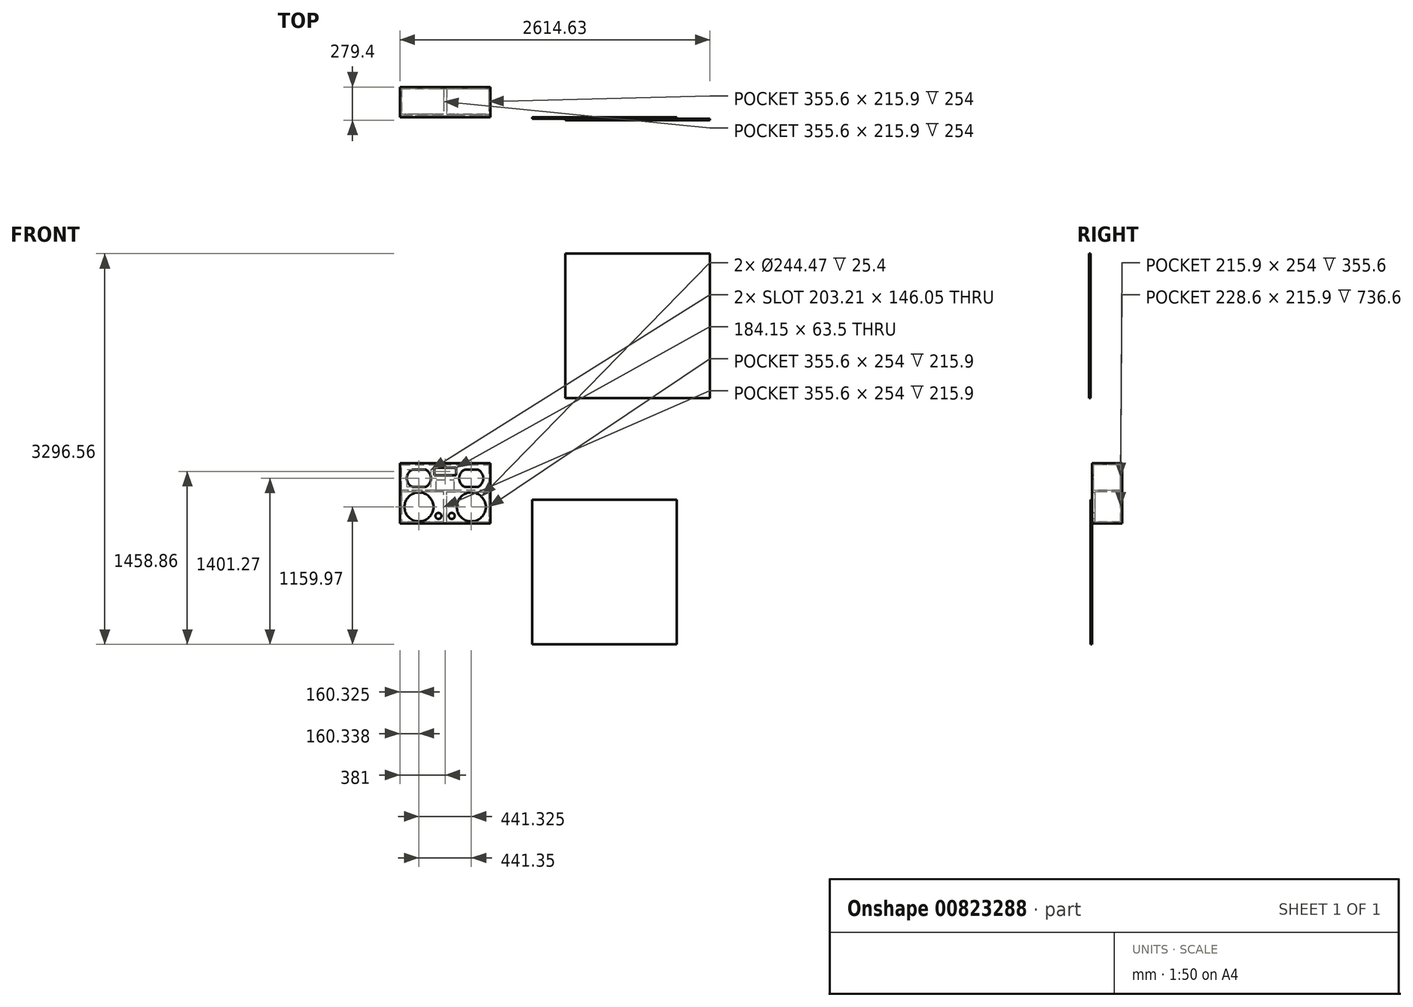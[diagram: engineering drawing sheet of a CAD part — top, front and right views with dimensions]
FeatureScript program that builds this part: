
annotation { "Feature Type Name" : "Feature", "Feature Type Description" : "" }
export const myFeature = defineFeature(function(context is Context, id is Id, definition is map)
    precondition{}
    {
        {
            var Q0;
            Q0=qCreatedBy(makeId("Front.planeOp"),FACE);
            var sketch = newSketch(context, id + "F0", { "sketchPlane" : qUnion([Q0])});
            skLineSegment(sketch, "E0.bottom", {"start": v(381, 254) * mm, "end": v(-381, 254) * mm});
            skLineSegment(sketch, "E0.top", {"start": v(381, -254) * mm, "end": v(-381, -254) * mm});
            skLineSegment(sketch, "E0.left", {"start": v(381, 254) * mm, "end": v(381, -254) * mm});
            skLineSegment(sketch, "E0.right", {"start": v(-381, 254) * mm, "end": v(-381, -254) * mm});
            skPoint(sketch, "E0.middle", {"position": v(0, 0) * mm});
            skSolve(sketch);
        }
        {
            var Q0;
            Q0 = qSketchRegion(id + "F0", true);
            extrude(context, id + "F1", {"entities" : qUnion([Q0]), "oppositeDirection" : true, "depth" : 12.7 * mm, "offsetDistance" : 25.4 * mm});
        }
        {
            var Q0;
            Q0=makeQuery(id+"F1.opExtrude","CAP_FACE",FACE,{"disambiguationData":[OSD([sQuery(id+"F0.wireOp",EDGE,"E0.bottom"),sQuery(id+"F0.wireOp",EDGE,"E0.top"),sQuery(id+"F0.wireOp",EDGE,"E0.left"),sQuery(id+"F0.wireOp",EDGE,"E0.right")])],"isStart":false});
            var sketch = newSketch(context, id + "F2", { "sketchPlane" : qUnion([Q0])});
            skLineSegment(sketch, "E1", {"start": v(368.3, 241.3) * mm, "end": v(-368.3, 241.3) * mm});
            skLineSegment(sketch, "E2", {"start": v(-381, 254) * mm, "end": v(-381, -254) * mm});
            skLineSegment(sketch, "E3", {"start": v(-381, -254) * mm, "end": v(381, -254) * mm});
            skLineSegment(sketch, "E4", {"start": v(381, -254) * mm, "end": v(381, 254) * mm});
            skLineSegment(sketch, "E5", {"start": v(381, 254) * mm, "end": v(-381, 254) * mm});
            skLineSegment(sketch, "E6", {"start": v(-12.7, -241.3) * mm, "end": v(-368.3, -241.3) * mm});
            skLineSegment(sketch, "E7", {"start": v(12.7, -241.3) * mm, "end": v(368.3, -241.3) * mm});
            skLineSegment(sketch, "E8", {"start": v(-368.3, 12.7) * mm, "end": v(-368.3, -241.3) * mm});
            skLineSegment(sketch, "E9", {"start": v(368.3, 12.7) * mm, "end": v(368.3, -241.3) * mm});
            skLineSegment(sketch, "E10", {"start": v(-12.7, -241.3) * mm, "end": v(-12.7, 12.7) * mm});
            skLineSegment(sketch, "E11", {"start": v(-12.7, 12.7) * mm, "end": v(-368.3, 12.7) * mm});
            skLineSegment(sketch, "E12", {"start": v(12.7, -241.3) * mm, "end": v(12.7, 12.7) * mm});
            skLineSegment(sketch, "E13", {"start": v(12.7, 12.7) * mm, "end": v(368.3, 12.7) * mm});
            skLineSegment(sketch, "E14", {"start": v(-368.3, 241.3) * mm, "end": v(-368.3, 25.4) * mm});
            skLineSegment(sketch, "E15", {"start": v(-368.3, 25.4) * mm, "end": v(368.3, 25.4) * mm});
            skLineSegment(sketch, "E16", {"start": v(368.3, 25.4) * mm, "end": v(368.3, 241.3) * mm});
            skSolve(sketch);
        }
        {
            var Q0;
            Q0 = qSketchRegion(id + "F2", true);
            extrude(context, id + "F3", {"entities" : qUnion([Q0]), "operationType" : NewBodyOperationType.ADD, "depth" : 228.6 * mm, "offsetDistance" : 25.4 * mm});
        }
        {
            var Q0;
            Q0=makeQuery(id+"F3.boolean.opBoolean","SPLIT",FACE,{"disambiguationData":[TD([makeQuery(id+"F3.opExtrude","SWEPT_FACE",FACE,{"disambiguationData":[OSD([sQuery(id+"F2.wireOp",EDGE,"E6")])]})])],"derivedFrom":makeQuery(id+"F1.opExtrude","CAP_FACE",FACE,{"disambiguationData":[OSD([sQuery(id+"F0.wireOp",EDGE,"E0.bottom"),sQuery(id+"F0.wireOp",EDGE,"E0.top"),sQuery(id+"F0.wireOp",EDGE,"E0.left"),sQuery(id+"F0.wireOp",EDGE,"E0.right")])],"isStart":false})});
            var sketch = newSketch(context, id + "F4", { "sketchPlane" : qUnion([Q0])});
            skLineSegment(sketch, "E17", {"start": v(-368.3, 12.7) * mm, "end": v(-368.3, -241.3) * mm});
            skLineSegment(sketch, "E18", {"start": v(-368.3, -241.3) * mm, "end": v(-12.7, -241.3) * mm});
            skLineSegment(sketch, "E19", {"start": v(-12.7, -241.3) * mm, "end": v(-12.7, 12.7) * mm});
            skLineSegment(sketch, "E20", {"start": v(-12.7, 12.7) * mm, "end": v(-368.3, 12.7) * mm});
            skSolve(sketch);
        }
        {
            var Q0;
            Q0=makeQuery(id+"F4.imprint","IMPRINT",FACE,{"disambiguationData":[TD([[makeQuery(id+"F4.imprint","IMPRINT",EDGE,{"derivedFrom":sQuery(id+"F4.wireOp",EDGE,"E17")}),1.0]])]});
            extrude(context, id + "F5", {"entities" : qUnion([Q0]), "operationType" : NewBodyOperationType.ADD, "depth" : 12.7 * mm, "offsetDistance" : 25.4 * mm});
        }
        {
            var Q0;
            Q0=makeQuery(id+"F3.boolean.opBoolean","SPLIT",FACE,{"disambiguationData":[TD([makeQuery(id+"F3.opExtrude","SWEPT_FACE",FACE,{"disambiguationData":[OSD([sQuery(id+"F2.wireOp",EDGE,"E7")])]})])],"derivedFrom":makeQuery(id+"F1.opExtrude","CAP_FACE",FACE,{"disambiguationData":[OSD([sQuery(id+"F0.wireOp",EDGE,"E0.bottom"),sQuery(id+"F0.wireOp",EDGE,"E0.top"),sQuery(id+"F0.wireOp",EDGE,"E0.left"),sQuery(id+"F0.wireOp",EDGE,"E0.right")])],"isStart":false})});
            extrude(context, id + "F6", {"entities" : qUnion([Q0]), "operationType" : NewBodyOperationType.ADD, "depth" : 12.7 * mm, "offsetDistance" : 25.4 * mm});
        }
        {
            var Q0;
            Q0=makeQuery(id+"F1.opExtrude","CAP_FACE",FACE,{"disambiguationData":[OSD([sQuery(id+"F0.wireOp",EDGE,"E0.bottom"),sQuery(id+"F0.wireOp",EDGE,"E0.top"),sQuery(id+"F0.wireOp",EDGE,"E0.left"),sQuery(id+"F0.wireOp",EDGE,"E0.right")])],"isStart":true});
            var sketch = newSketch(context, id + "F7", { "sketchPlane" : qUnion([Q0])});
            skCircle(sketch, "E21", {"center": v(-220.66, -114.3) * mm, "radius": 122.24 * mm});
            skCircle(sketch, "E22.MirrorC", {"center": v(220.66, -114.3) * mm, "radius": 122.24 * mm});
            skSolve(sketch);
        }
        {
            var Q0;
            Q0 = qSketchRegion(id + "F7", true);
            extrude(context, id + "F8", {"entities" : qUnion([Q0]), "operationType" : NewBodyOperationType.REMOVE, "oppositeDirection" : true, "depth" : 25.4 * mm, "offsetDistance" : 25.4 * mm});
        }
        {
            var Q0;
            Q0=makeQuery(id+"F1.opExtrude","CAP_FACE",FACE,{"disambiguationData":[OSD([sQuery(id+"F0.wireOp",EDGE,"E0.bottom"),sQuery(id+"F0.wireOp",EDGE,"E0.top"),sQuery(id+"F0.wireOp",EDGE,"E0.left"),sQuery(id+"F0.wireOp",EDGE,"E0.right")])],"isStart":true});
            var sketch = newSketch(context, id + "F9", { "sketchPlane" : qUnion([Q0])});
            skCircle(sketch, "E23", {"center": v(-56.03, -190.18) * mm, "radius": 25.4 * mm});
            skCircle(sketch, "E24.MirrorC", {"center": v(56.03, -190.18) * mm, "radius": 25.4 * mm});
            skSolve(sketch);
        }
        {
            var Q0;
            Q0 = qSketchRegion(id + "F9", true);
            extrude(context, id + "F10", {"entities" : qUnion([Q0]), "operationType" : NewBodyOperationType.REMOVE, "oppositeDirection" : true, "depth" : 25.4 * mm, "offsetDistance" : 25.4 * mm});
        }
        {
            var Q0;
            Q0=makeQuery(id+"F1.opExtrude","CAP_FACE",FACE,{"disambiguationData":[OSD([sQuery(id+"F0.wireOp",EDGE,"E0.bottom"),sQuery(id+"F0.wireOp",EDGE,"E0.top"),sQuery(id+"F0.wireOp",EDGE,"E0.left"),sQuery(id+"F0.wireOp",EDGE,"E0.right")])],"isStart":true});
            var sketch = newSketch(context, id + "F11", { "sketchPlane" : qUnion([Q0])});
            skLineSegment(sketch, "E25", {"start": v(0, 216.34) * mm, "end": v(-92.07, 216.34) * mm});
            skLineSegment(sketch, "E26", {"start": v(0, 152.84) * mm, "end": v(-92.07, 152.84) * mm});
            skLineSegment(sketch, "E27", {"start": v(-92.07, 152.84) * mm, "end": v(-92.07, 216.34) * mm});
            skLineSegment(sketch, "E28.MirrorCS", {"start": v(0, 216.34) * mm, "end": v(92.08, 216.34) * mm});
            skLineSegment(sketch, "E29.MirrorCS", {"start": v(92.08, 152.84) * mm, "end": v(92.08, 216.34) * mm});
            skLineSegment(sketch, "E30.MirrorCS", {"start": v(0, 152.84) * mm, "end": v(92.08, 152.84) * mm});
            skSolve(sketch);
        }
        {
            var Q0;
            Q0=makeQuery(id+"F11.imprint","IMPRINT",FACE,{"disambiguationData":[TD([[makeQuery(id+"F11.imprint","IMPRINT",EDGE,{"derivedFrom":sQuery(id+"F11.wireOp",EDGE,"E25")}),1.0]])]});
            extrude(context, id + "F12", {"entities" : qUnion([Q0]), "operationType" : NewBodyOperationType.REMOVE, "oppositeDirection" : true, "depth" : 25.4 * mm, "offsetDistance" : 25.4 * mm});
        }
        {
            var Q0;
            Q0=makeQuery(id+"F7.imprint","IMPRINT",FACE,{"disambiguationData":[TD([[makeQuery(id+"F7.imprint","IMPRINT",EDGE,{"derivedFrom":sQuery(id+"F7.wireOp",EDGE,"E21")}),-1.0]])]});
            var sketch = newSketch(context, id + "F13", { "sketchPlane" : qUnion([Q0])});
            skLineSegment(sketch, "E31", {"start": v(-220.68, 53.97) * mm, "end": v(-277.83, 53.97) * mm});
            skLineSegment(sketch, "E32", {"start": v(-220.68, 53.97) * mm, "end": v(-163.53, 53.97) * mm});
            skLineSegment(sketch, "E33", {"start": v(-220.68, 200.02) * mm, "end": v(-163.53, 200.02) * mm});
            skLineSegment(sketch, "E34", {"start": v(-220.68, 200.02) * mm, "end": v(-277.83, 200.02) * mm});
            skArc(sketch, "E35", {"start": v(-163.53, 53.97) * mm, "mid": v(-119.07, 127) * mm, "end": v(-163.53, 200.02) * mm});
            skArc(sketch, "E36.MirrorCS", {"start": v(-277.83, 53.97) * mm, "mid": v(-322.28, 127) * mm, "end": v(-277.83, 200.02) * mm});
            skArc(sketch, "E37.MirrorCS", {"start": v(163.53, 53.97) * mm, "mid": v(119.07, 127) * mm, "end": v(163.53, 200.02) * mm});
            skLineSegment(sketch, "E38.MirrorCS", {"start": v(220.68, 200.02) * mm, "end": v(163.53, 200.02) * mm});
            skLineSegment(sketch, "E39.MirrorCS", {"start": v(220.68, 200.02) * mm, "end": v(277.83, 200.02) * mm});
            skArc(sketch, "E40.MirrorCS", {"start": v(277.83, 53.97) * mm, "mid": v(322.28, 127) * mm, "end": v(277.83, 200.02) * mm});
            skLineSegment(sketch, "E41.MirrorCS", {"start": v(220.68, 53.97) * mm, "end": v(277.83, 53.97) * mm});
            skLineSegment(sketch, "E42.MirrorCS", {"start": v(220.68, 53.97) * mm, "end": v(163.53, 53.97) * mm});
            skSolve(sketch);
        }
        {
            var Q0;
            Q0 = qSketchRegion(id + "F13", true);
            extrude(context, id + "F14", {"entities" : qUnion([Q0]), "operationType" : NewBodyOperationType.REMOVE, "oppositeDirection" : true, "depth" : 12.7 * mm, "offsetDistance" : 25.4 * mm});
        }
        {
            var Q0;
            Q0=makeQuery(id+"F3.boolean.opBoolean","MERGE",FACE,{"derivedFrom":[makeQuery(id+"F1.opExtrude","SWEPT_FACE",FACE,{"disambiguationData":[OSD([sQuery(id+"F0.wireOp",EDGE,"E0.right")])]}),makeQuery(id+"F3.opExtrude","SWEPT_FACE",FACE,{"disambiguationData":[OSD([sQuery(id+"F2.wireOp",EDGE,"E4")])]})]});
            var sketch = newSketch(context, id + "F15", { "sketchPlane" : qUnion([Q0])});
            skLineSegment(sketch, "E43", {"start": v(-254, -254) * mm, "end": v(-254, 254) * mm});
            skLineSegment(sketch, "E44", {"start": v(-254, 254) * mm, "end": v(-241.3, 254) * mm});
            skLineSegment(sketch, "E45", {"start": v(-241.3, 254) * mm, "end": v(-241.3, -254) * mm});
            skLineSegment(sketch, "E46", {"start": v(-241.3, -254) * mm, "end": v(-254, -254) * mm});
            skSolve(sketch);
        }
        {
            var Q0;
            Q0 = qSketchRegion(id + "F15", true);
            extrude(context, id + "F16", {"entities" : qUnion([Q0]), "operationType" : NewBodyOperationType.ADD, "oppositeDirection" : true, "depth" : 762 * mm, "offsetDistance" : 25.4 * mm});
        }
        {
            var Q0;
            Q0=makeQuery(id+"F16.boolean.opBoolean","SPLIT",FACE,{"disambiguationData":[TD([makeQuery(id+"F3.opExtrude","SWEPT_FACE",FACE,{"disambiguationData":[OSD([sQuery(id+"F2.wireOp",EDGE,"E1")])]})])],"derivedFrom":makeQuery(id+"F16.opExtrude","SWEPT_FACE",FACE,{"disambiguationData":[OSD([sQuery(id+"F15.wireOp",EDGE,"E45")])]})});
            var sketch = newSketch(context, id + "F17", { "sketchPlane" : qUnion([Q0])});
            skLineSegment(sketch, "E47", {"start": v(0, 25.4) * mm, "end": v(-76.2, 25.4) * mm});
            skLineSegment(sketch, "E48", {"start": v(-76.2, 25.4) * mm, "end": v(-76.2, 69.85) * mm});
            skLineSegment(sketch, "E49.MirrorCS", {"start": v(0, 25.4) * mm, "end": v(76.2, 25.4) * mm});
            skLineSegment(sketch, "E50.MirrorCS", {"start": v(76.2, 25.4) * mm, "end": v(76.2, 69.85) * mm});
            skLineSegment(sketch, "E51.MirrorCS", {"start": v(-76.2, 114.3) * mm, "end": v(-76.2, 69.85) * mm});
            skLineSegment(sketch, "E52.MirrorCS", {"start": v(76.2, 114.3) * mm, "end": v(76.2, 69.85) * mm});
            skLineSegment(sketch, "E53", {"start": v(-76.2, 114.3) * mm, "end": v(76.2, 114.3) * mm});
            skSolve(sketch);
        }
        {
            var Q0;
            Q0 = qSketchRegion(id + "F17", true);
            extrude(context, id + "F18", {"entities" : qUnion([Q0]), "operationType" : NewBodyOperationType.REMOVE, "oppositeDirection" : true, "depth" : 12.7 * mm, "offsetDistance" : 25.4 * mm});
        }
        {
            var Q0;
            Q0=makeQuery(id+"F1.opExtrude","CAP_FACE",FACE,{"disambiguationData":[OSD([sQuery(id+"F0.wireOp",EDGE,"E0.bottom"),sQuery(id+"F0.wireOp",EDGE,"E0.top"),sQuery(id+"F0.wireOp",EDGE,"E0.left"),sQuery(id+"F0.wireOp",EDGE,"E0.right")])],"isStart":true});
            var sketch = newSketch(context, id + "F19", { "sketchPlane" : qUnion([Q0])});
            skLineSegment(sketch, "E54", {"start": v(735.62, -1274.27) * mm, "end": v(1954.82, -1274.27) * mm});
            skLineSegment(sketch, "E55", {"start": v(1954.82, -1274.27) * mm, "end": v(1954.82, -55.07) * mm});
            skLineSegment(sketch, "E56", {"start": v(1954.82, -55.07) * mm, "end": v(735.62, -55.07) * mm});
            skLineSegment(sketch, "E57", {"start": v(735.62, -55.07) * mm, "end": v(735.62, -1274.27) * mm});
            skSolve(sketch);
        }
        {
            var Q0;
            Q0=makeQuery(id+"F19.imprint","IMPRINT",FACE,{"disambiguationData":[TD([[makeQuery(id+"F19.imprint","IMPRINT",EDGE,{"derivedFrom":sQuery(id+"F19.wireOp",EDGE,"E54")}),1.0]])]});
            extrude(context, id + "F20", {"entities" : qUnion([Q0]), "depth" : 12.7 * mm, "offsetDistance" : 25.4 * mm});
        }
        {
            var Q0;
            Q0=makeQuery(id+"F20.opExtrude","CAP_FACE",FACE,{"disambiguationData":[OSD([sQuery(id+"F19.wireOp",EDGE,"E54"),sQuery(id+"F19.wireOp",EDGE,"E55"),sQuery(id+"F19.wireOp",EDGE,"E56"),sQuery(id+"F19.wireOp",EDGE,"E57")])],"isStart":false});
            var sketch = newSketch(context, id + "F21", { "sketchPlane" : qUnion([Q0])});
            skLineSegment(sketch, "E58", {"start": v(1014.43, 803.09) * mm, "end": v(2233.63, 803.09) * mm});
            skLineSegment(sketch, "E59", {"start": v(2233.63, 803.09) * mm, "end": v(2233.63, 2022.29) * mm});
            skLineSegment(sketch, "E60", {"start": v(2233.63, 2022.29) * mm, "end": v(1014.43, 2022.29) * mm});
            skLineSegment(sketch, "E61", {"start": v(1014.43, 2022.29) * mm, "end": v(1014.43, 803.09) * mm});
            skSolve(sketch);
        }
        {
            var Q0;
            Q0 = qSketchRegion(id + "F21", true);
            extrude(context, id + "F22", {"entities" : qUnion([Q0]), "depth" : 12.7 * mm, "offsetDistance" : 25.4 * mm});
        }
    });
